# Revit family: RN 81168 Optipress-Aquaplus-Gruppo valvola d'arresto e sicurezza SW
name_source: partatom
category: Rohrzubehör
units: mm (PartAtom-declared; Revit-internal decimal feet)

## family parameters
Arbeitsebenenbasiert = Nein
Beim Laden mit Abzugskörper schneiden = Nein
Bemaßung runder Anschluss = Durchmesser verwenden
Gemeinsam genutzt = Nein
Immer vertikal = Ja
Teiletyp = Ventil - Zerlegung in

## types (5) — shared parameters
1.010.00.2 Number of the part of the guideline = 17
1.010.00.3 Issue date (month) of the guideline = 201601
1.010.00.4 Manufacturer name = R. Nussbaum AG
1.010.00.5 Revision date of the file = 20190528
1.100.00.3 Sort number for display sequence = 5
1.100.00.4 Product designation = Elementi di sicurezza
1.960/3L.00.8 Link (URL) = https://www.nussbaum.ch
17.700.00.4 valve assembly type = 6
17.700.00.7 maximum operating temperature TB [°C] = 90
17.700.00.8 maximum operating pressure(working pressure) ps [1.0 · 105 Pa] = 16
Connector Visibility = Nein
EnclosingSpace Visibility = Nein

## per-type parameters (varying)
| type | 1.800.00.3 BS number | 1.810.00.3 Manufacturer’s reference number | 1.810.00.4 DATANORM number | 1.810.00.5 StLB number | 1.810.00.6 GTIN number | 17.700.00.30 product description | 17.700.00.5 nominal size DN | 17.700.00.6 kvs-value [m3/h] | CONNECTOR0_DIAMETER_dZ_0r | CONNECTOR0_dZ_00 | CONNECTOR0_dZ_01 | CONNECTOR0_ref_dZ | CONNECTOR1_DIAMETER_dZ_0r | CONNECTOR1_dZ_00 | CONNECTOR1_dZ_01 | CONNECTOR1_ref_dZ | CONNECTOR2_DIAMETER_dZ_0r | CONNECTOR2_dZ_00 | CONNECTOR2_ref_dX | R. Nussbaum AG 81168.24 it Visibility | R. Nussbaum AG 81168.25 it Visibility | R. Nussbaum AG 81168.26 it Visibility | R. Nussbaum AG 81168.27 it Visibility | R. Nussbaum AG 81168.30 it Visibility |
| DN 20 | 005019???0000000000000000000020070000000000000000100000000 | 81168.24 | 81168.24 | 612.414 | 7612945737472 | 81168.24, OP-A-Gruppo valv. arresto/sicurezza SW, per scaldacqua a colonna, DN=20 | 20 | 10.8 | 20 mm | 59 mm  [stored 0.19357 ft] | 35 mm | 35 mm | 20 mm | 43 mm | 67 mm | 43 mm | 20 mm | 16 mm  [stored 0.0524934 ft] | 70 mm | Ja | Nein | Nein | Nein | Nein |
| DN 25 | 005019???0000000000000000000020070000000000000000200000000 | 81168.25 | 81168.25 | 612.415 | 7612945738226 | 81168.25, OP-A-Gruppo valv. arresto/sicurezza SW, per scaldacqua a colonna, DN=25 | 25 | 16.8 | 25 mm  [stored 0.082021 ft] | 64 mm | 40 mm | 40 mm | 25 mm  [stored 0.082021 ft] | 47 mm | 71 mm | 47 mm | 20 mm | 15 mm  [stored 0.0492126 ft] | 75 mm | Nein | Ja | Nein | Nein | Nein |
| DN 32 1 | 005019???0000000000000000000020070000000000000000300000000 | 81168.26 | 81168.26 | 612.416 | 7612945735508 | 81168.26, OP-A-Gruppo valv. arresto/sicurezza SW, per scaldacqua a colonna, DN=32 | 32 | 31.2 | 32 mm | 74 mm | 48 mm | 48 mm | 32 mm | 55 mm | 81 mm | 55 mm | 20 mm | 15 mm  [stored 0.0492126 ft] | 80 mm | Nein | Nein | Ja | Nein | Nein |
| DN 40 | 005019???0000000000000000000020070000000000000000400000000 | 81168.27 | 81168.27 | 612.417 | 7612945733863 | 81168.27, OP-A-Gruppo valv. arresto/sicurezza SW, per scaldacqua a colonna, DN=40 | 40 | 45 | 40 mm | 88 mm | 52 mm | 52 mm | 40 mm | 61 mm | 97 mm | 61 mm | 25 mm  [stored 0.082021 ft] | 17 mm | 80 mm | Nein | Nein | Nein | Ja | Nein |
| DN 32 | 005019???0000000000000000000020070000000000000000500000000 | 81168.30 | 81168.30 |  | 7612945735515 | 81168.30, OP-A-Gruppo valv. arresto/sicurezza SW, per scaldacqua a colonna, DN=32 | 32 | 31.2 | 32 mm | 73 mm | 47 mm | 47 mm | 32 mm | 56 mm | 82 mm | 56 mm | 25 mm  [stored 0.082021 ft] | 17 mm | 80 mm | Nein | Nein | Nein | Nein | Ja |

note: [stored X ft] marks values corroborated as IEEE doubles in the binary element streams (Revit-internal decimal feet)

## geometry (parser evidence)
native form markers: Sweep x3
no freeform markers — native parametric forms only
